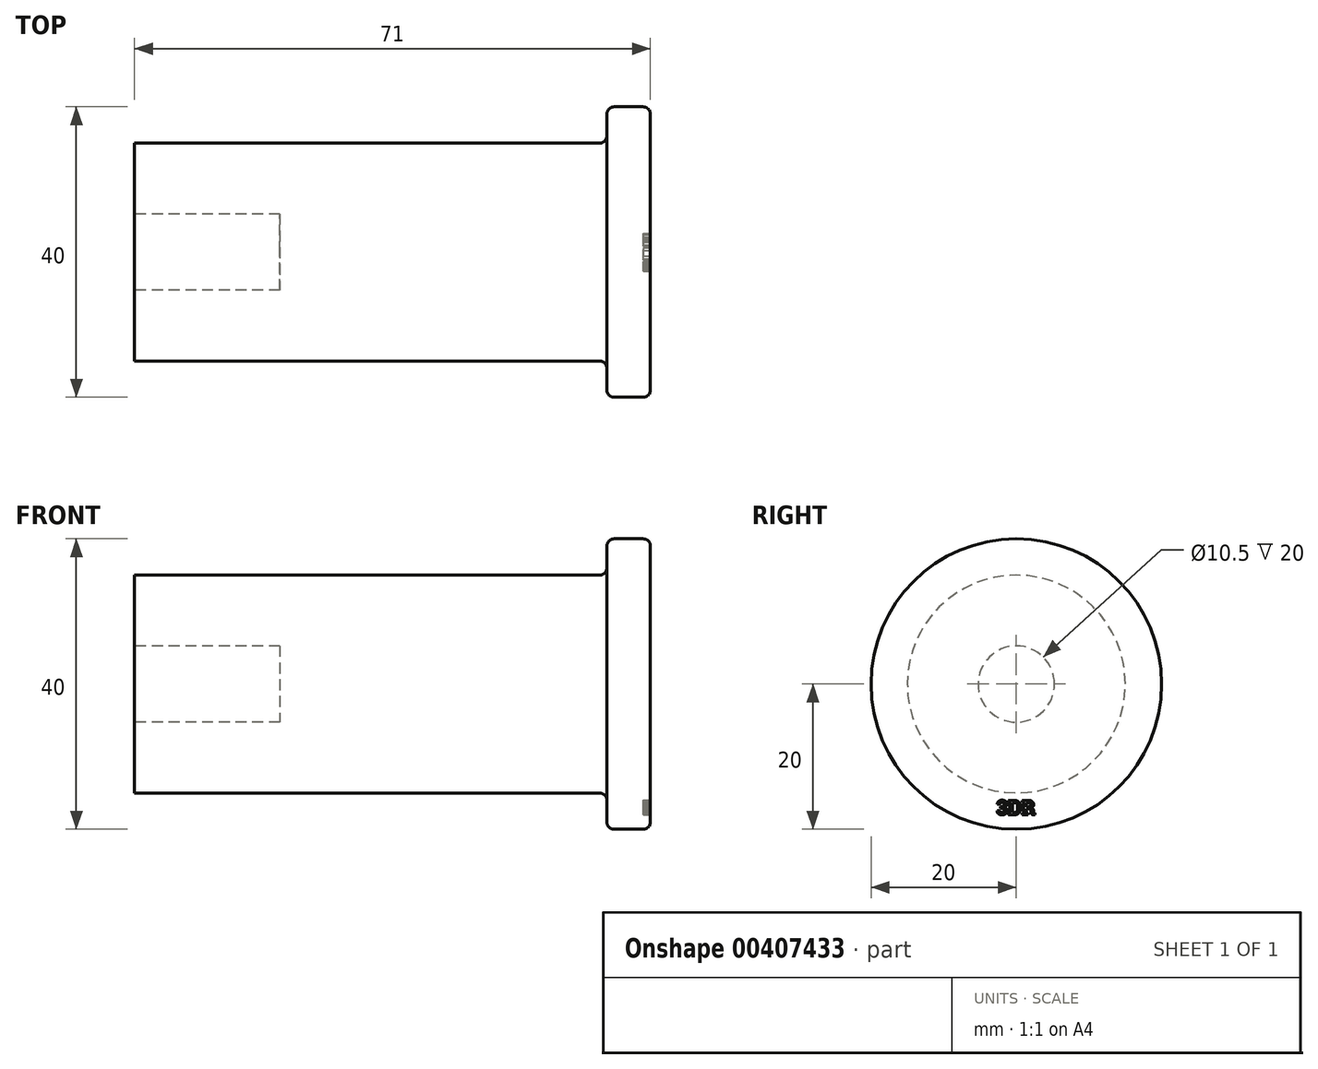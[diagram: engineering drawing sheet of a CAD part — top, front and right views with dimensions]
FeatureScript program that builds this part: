
annotation { "Feature Type Name" : "Feature", "Feature Type Description" : "" }
export const myFeature = defineFeature(function(context is Context, id is Id, definition is map)
    precondition{}
    {
        {
            var Q0;
            Q0=qCreatedBy(makeId("Front.planeOp"),FACE);
            var sketch = newSketch(context, id + "F0", { "sketchPlane" : qUnion([Q0])});
            skLineSegment(sketch, "E0", {"start": v(-32.5, 0) * mm, "end": v(32.5, 0) * mm, "construction": true});
            skLineSegment(sketch, "E1", {"start": v(-32.5, 15) * mm, "end": v(32.5, 15) * mm});
            skLineSegment(sketch, "E2", {"start": v(32.5, 15) * mm, "end": v(32.5, 20) * mm});
            skLineSegment(sketch, "E3", {"start": v(32.5, 20) * mm, "end": v(38.5, 20) * mm});
            skLineSegment(sketch, "E4", {"start": v(38.5, 20) * mm, "end": v(38.5, 0) * mm});
            skLineSegment(sketch, "E5", {"start": v(0, 18.7) * mm, "end": v(0, 8.7) * mm, "construction": true});
            skPoint(sketch, "E5.startSnap0", {"position": v(0, 15) * mm});
            skLineSegment(sketch, "E6", {"start": v(38.5, 0) * mm, "end": v(-32.5, 0) * mm});
            skLineSegment(sketch, "E7", {"start": v(-32.5, 15) * mm, "end": v(-32.5, 0) * mm});
            skSolve(sketch);
        }
        {
            var Q0;
            Q0 = qSketchRegion(id + "F0", true);
            var Q1;
            Q1=sQuery(id+"F0.wireOp",EDGE,"E6");
            revolve(context, id + "F1", {"entities" : qUnion([Q0]), "axis" : qUnion([Q1]), "revolveType" : RevolveType.FULL});
        }
        {
            var Q0;
            Q0=makeQuery(id+"F1.opRevolve","SWEPT_FACE",FACE,{"disambiguationData":[OSD([sQuery(id+"F0.wireOp",EDGE,"E7")])]});
            var sketch = newSketch(context, id + "F2", { "sketchPlane" : qUnion([Q0])});
            skCircle(sketch, "E8", {"center": v(0, 0) * mm, "radius": 5.25 * mm});
            skSolve(sketch);
        }
        {
            var Q0;
            Q0 = qSketchRegion(id + "F2", true);
            extrude(context, id + "F3", {"entities" : qUnion([Q0]), "operationType" : NewBodyOperationType.REMOVE, "oppositeDirection" : true, "depth" : 20 * mm});
        }
        {
            var Q0;
            Q0=makeQuery(id+"F1.opRevolve","SWEPT_EDGE",EDGE,{"disambiguationData":[OSD([sQuery(id+"F0.wireOp",EDGE,"E1"),sQuery(id+"F0.wireOp",EDGE,"E2")])]});
            var Q1;
            Q1=makeQuery(id+"F1.opRevolve","SWEPT_EDGE",EDGE,{"disambiguationData":[OSD([sQuery(id+"F0.wireOp",EDGE,"E3"),sQuery(id+"F0.wireOp",EDGE,"E4")])]});
            var Q2;
            Q2=makeQuery(id+"F1.opRevolve","SWEPT_EDGE",EDGE,{"disambiguationData":[OSD([sQuery(id+"F0.wireOp",EDGE,"E2"),sQuery(id+"F0.wireOp",EDGE,"E3")])]});
            fillet(context, id + "F4", {"entities" : qUnion([Q0, Q1, Q2]), "radius" : 1 * mm, "tangentPropagation" : true, "allowEdgeOverflow" : false});
        }
        {
            var Q0;
            Q0=makeQuery(id+"F1.opRevolve","SWEPT_FACE",FACE,{"disambiguationData":[OSD([sQuery(id+"F0.wireOp",EDGE,"E4")])]});
            var sketch = newSketch(context, id + "F5", { "sketchPlane" : qUnion([Q0])});
            skText(sketch, "E9", { "text": "3DR", "fontName": "RobotoSlab-Bold.ttf"});
            const initialGuessF5  = {"E9": [-0.00272, -0.018, 1, 0, 0.002]};
            skSetInitialGuess(sketch, initialGuessF5);
            skSolve(sketch);
        }
        {
            var Q0;
            Q0 = qSketchRegion(id + "F5", true);
            extrude(context, id + "F6", {"entities" : qUnion([Q0]), "operationType" : NewBodyOperationType.REMOVE, "oppositeDirection" : true, "depth" : 1 * mm});
        }
    });
